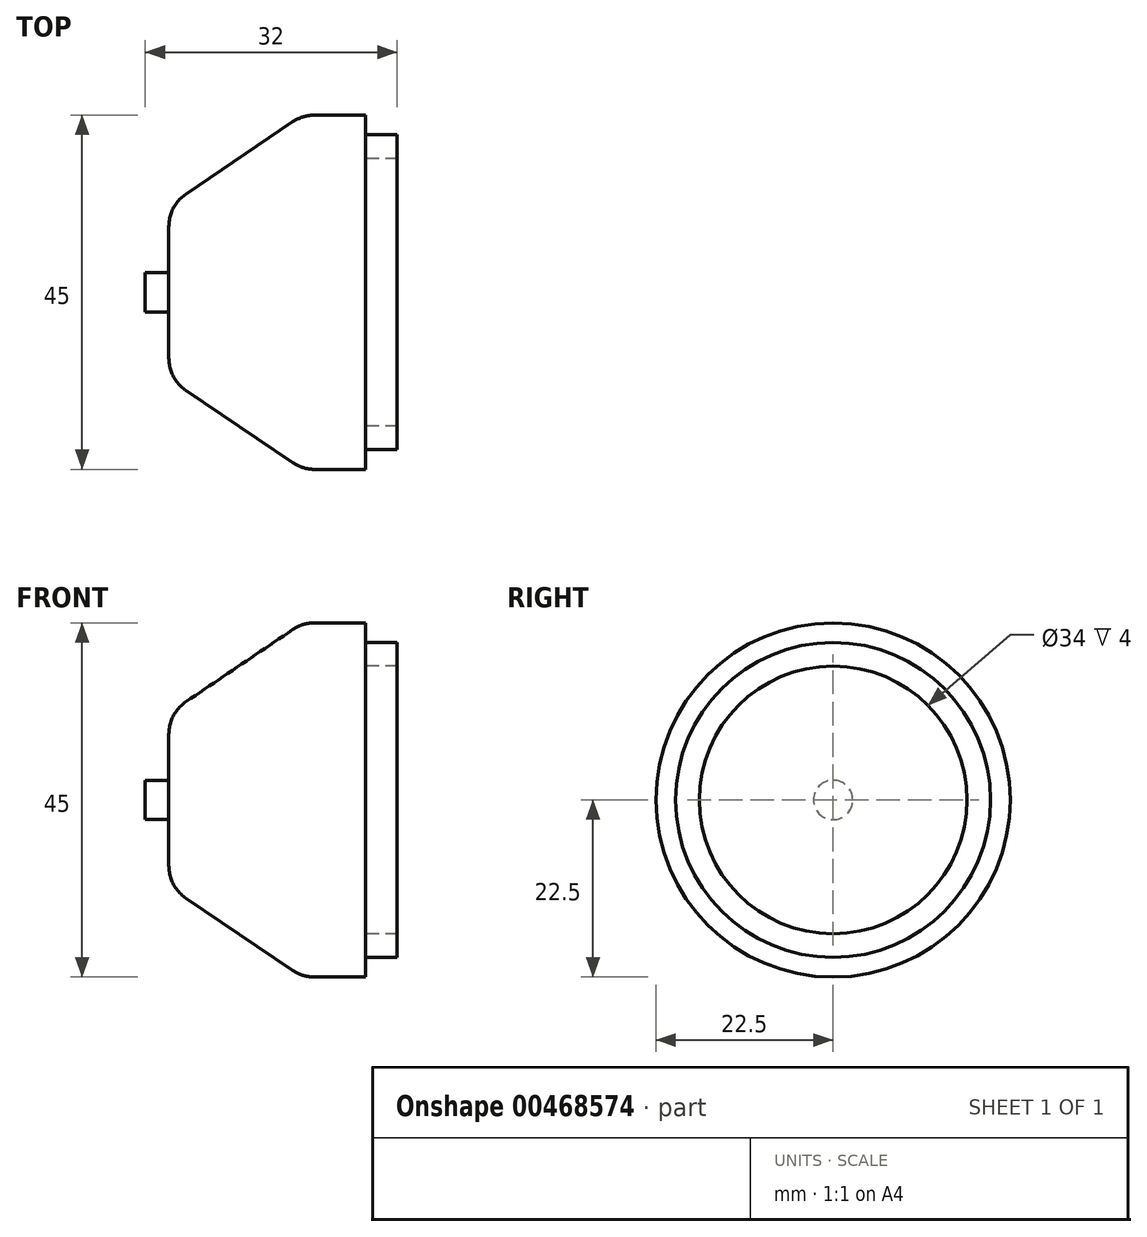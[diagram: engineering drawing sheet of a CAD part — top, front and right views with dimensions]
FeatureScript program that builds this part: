
annotation { "Feature Type Name" : "Feature", "Feature Type Description" : "" }
export const myFeature = defineFeature(function(context is Context, id is Id, definition is map)
    precondition{}
    {
        {
            var Q0;
            Q0=qCreatedBy(makeId("Front.planeOp"),FACE);
            var sketch = newSketch(context, id + "F0", { "sketchPlane" : qUnion([Q0])});
            skLineSegment(sketch, "E0", {"start": v(0, 0) * mm, "end": v(28, 0) * mm});
            skLineSegment(sketch, "E1", {"start": v(0, 0) * mm, "end": v(0, 2.5) * mm});
            skLineSegment(sketch, "E2", {"start": v(0, 2.5) * mm, "end": v(3, 2.5) * mm});
            skLineSegment(sketch, "E3", {"start": v(3, 2.5) * mm, "end": v(3, 8.35) * mm});
            skPoint(sketch, "E4", {"position": v(28, 0) * mm});
            skLineSegment(sketch, "E5", {"start": v(28, 0) * mm, "end": v(28, 22.5) * mm});
            skLineSegment(sketch, "E6", {"start": v(28, 22.5) * mm, "end": v(21.53, 22.5) * mm});
            skLineSegment(sketch, "E7", {"start": v(18.73, 21.64) * mm, "end": v(5.2, 12.49) * mm});
            skPoint(sketch, "E8", {"position": v(28, 20) * mm});
            skLineSegment(sketch, "E9", {"start": v(28, 20) * mm, "end": v(32, 20) * mm});
            skLineSegment(sketch, "E10", {"start": v(32, 20) * mm, "end": v(32, 17) * mm});
            skLineSegment(sketch, "E11", {"start": v(32, 17) * mm, "end": v(28, 17) * mm});
            skPoint(sketch, "E12.visualSharp", {"position": v(20, 22.5) * mm});
            skArc(sketch, "E12.filletArc", {"start": v(21.53, 22.5) * mm, "mid": v(20.07, 22.28) * mm, "end": v(18.73, 21.64) * mm});
            skPoint(sketch, "E13.visualSharp", {"position": v(3, 11) * mm});
            skArc(sketch, "E13.filletArc", {"start": v(5.2, 12.49) * mm, "mid": v(3.58, 10.7) * mm, "end": v(3, 8.35) * mm});
            skSolve(sketch);
        }
        {
            var Q0;
            Q0 = qSketchRegion(id + "F0", true);
            var Q1;
            Q1=sQuery(id+"F0.wireOp",EDGE,"E0");
            revolve(context, id + "F1", {"surfaceOperationType" : NewSurfaceOperationType.NEW, "entities" : qUnion([Q0]), "axis" : qUnion([Q1]), "revolveType" : RevolveType.FULL});
        }
    });
